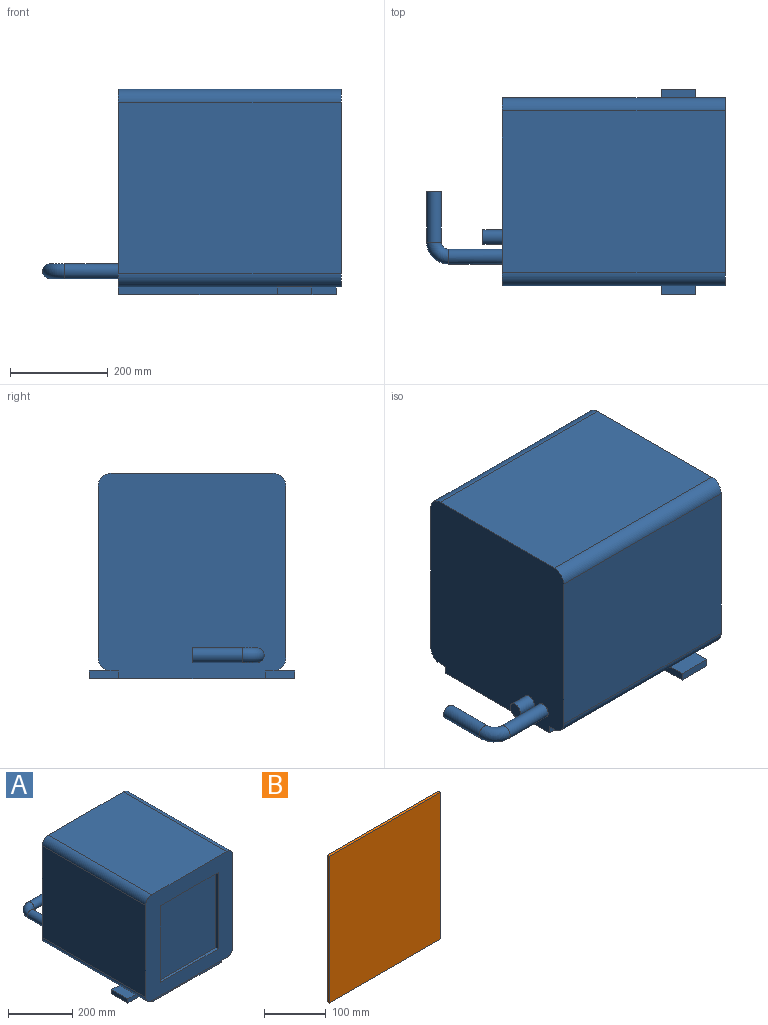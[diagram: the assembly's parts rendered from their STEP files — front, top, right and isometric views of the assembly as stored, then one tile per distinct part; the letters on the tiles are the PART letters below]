
ASSEMBLY  parts=2 mates=1
PART A: 37 faces, bbox 420x614.2x420 mm
  f0: plane 404x384mm, normal (0,-1,0), area 80244.4mm2, adj f6,f8,f9,f10,f11,f12,f13,f16
  f1: plane 70.5x45mm, normal (0,0,1), area 3172.5mm2, adj f3,f6,f18,f21
  f2: plane 445.5x420mm, normal (0,0,-1), area 142110mm2, adj f3,f4,f5,f14,f15,f17,f18,f20
  f3: plane 70.5x16mm, normal (-1,0,0), area 1128mm2, adj f1,f2,f18,f21
  f4: plane 70.5x16mm, normal (1,0,0), area 1128mm2, adj f2,f7,f15,f24
  f5: plane 420x384mm, normal (0,1,0), area 157896.5mm2, adj f2,f6,f8,f9,f10,f11,f12,f13
  f6: cylinder r=27mm len=455.5mm, axis (0,-1,0), area 19318.4mm2, adj f0,f1,f5,f13,f16,f19
  f7: plane 70.5x45mm, normal (0,0,1), area 3172.5mm2, adj f4,f8,f15,f24
  f8: cylinder r=27mm len=455.5mm, axis (0,-1,0), area 19318.4mm2, adj f0,f5,f7,f9,f16,f22
  f9: plane 455.5x350mm, normal (1,0,0), area 159425mm2, adj f0,f5,f8,f10
  f10: cylinder r=27mm len=455.5mm, axis (0,-1,0), area 19318.4mm2, adj f0,f5,f9,f11
  f11: plane 455.5x330mm, normal (0,0,1), area 150315mm2, adj f0,f5,f10,f12
  f12: cylinder r=27mm len=455.5mm, axis (0,-1,0), area 19318.4mm2, adj f0,f5,f11,f13
  f13: plane 455.5x350mm, normal (-1,0,0), area 159425mm2, adj f0,f5,f6,f12
  f14: plane 50x16mm, normal (1,0,0), area 800mm2, adj f2,f15,f16,f36
  f15: plane 60x16mm, normal (0,-1,0), area 960mm2, adj f2,f4,f7,f14,f16
  f16: plane 330x60mm, normal (0,0,-1), area 4800mm2, adj f0,f6,f8,f14,f15,f17,f18,f36
  f17: plane 50x16mm, normal (-1,0,0), area 800mm2, adj f2,f16,f18,f36
  f18: plane 60x16mm, normal (0,-1,0), area 960mm2, adj f1,f2,f3,f16,f17
  f19: plane 325x15mm, normal (0,0,-1), area 4875mm2, adj f5,f6,f20,f21
  f20: plane 325x16mm, normal (-1,0,0), area 5200mm2, adj f2,f5,f19,f21
  f21: plane 60x16mm, normal (0,1,0), area 960mm2, adj f1,f2,f3,f19,f20
  f22: plane 325x15mm, normal (0,0,-1), area 4875mm2, adj f5,f8,f23,f24
  f23: plane 325x16mm, normal (1,0,0), area 5200mm2, adj f2,f5,f22,f24
  f24: plane 60x16mm, normal (0,1,0), area 960mm2, adj f2,f4,f7,f22,f23
  f25: plane 254.78x10mm, normal (0,0,1), area 2547.8mm2, adj f0,f26,f28,f29
  f26: plane 291.49x10mm, normal (-1,0,0), area 2914.9mm2, adj f0,f25,f27,f29
  f27: plane 254.78x10mm, normal (0,0,-1), area 2547.8mm2, adj f0,f26,f28,f29
  f28: plane 291.49x10mm, normal (1,0,0), area 2914.9mm2, adj f0,f25,f27,f29
  f29: plane 291.49x254.78mm, normal (0,-1,0), area 74265.8mm2, adj f25,f26,f27,f28
  f30: cylinder r=15mm len=40mm, axis (0,-1,0), area 3769.9mm2, adj f5,f31
  f31: plane 30x30mm, normal (0,1,0), area 706.9mm2, adj f30
  f32: cylinder r=15mm len=110mm, axis (0,-1,0), area 10367.3mm2, adj f5,f34
  f33: plane 30x30mm, normal (1,0,0), area 706.9mm2, adj f35
  f34: torus R=30mm, axis (0,0,-1), area 4441.3mm2, adj f32,f35
  f35: cylinder r=15mm len=102.3mm, axis (1,0,0), area 9641.5mm2, adj f33,f34
  f36: plane 300x16mm, normal (0,-1,0), area 4800mm2, adj f2,f14,f16,f17
PART B: 6 faces, bbox 254.8x5x291.5 mm
  f0: plane 254.78x5mm, normal (0,0,-1), area 1273.9mm2, adj f1,f3,f4,f5
  f1: plane 291.49x5mm, normal (1,0,0), area 1457.4mm2, adj f0,f2,f4,f5
  f2: plane 254.78x5mm, normal (0,0,1), area 1273.9mm2, adj f1,f3,f4,f5
  f3: plane 291.49x5mm, normal (-1,0,0), area 1457.4mm2, adj f0,f2,f4,f5
  f4: plane 291.49x254.78mm, normal (0,-1,0), area 74265.8mm2, adj f0,f1,f2,f3
  f5: plane 291.49x254.78mm, normal (0,1,0), area 74265.8mm2, adj f0,f1,f2,f3
PLACE A rot(axis=(0,0,1),90deg) t=(10,0,4.71)mm
PLACE B rot(axis=(0.71,0.71,0),180deg) t=(-5,0,-4.71)mm
MATE fastened B.f4 <-> A.f29  axis (-1,0,0) through (0,0,0)mm
